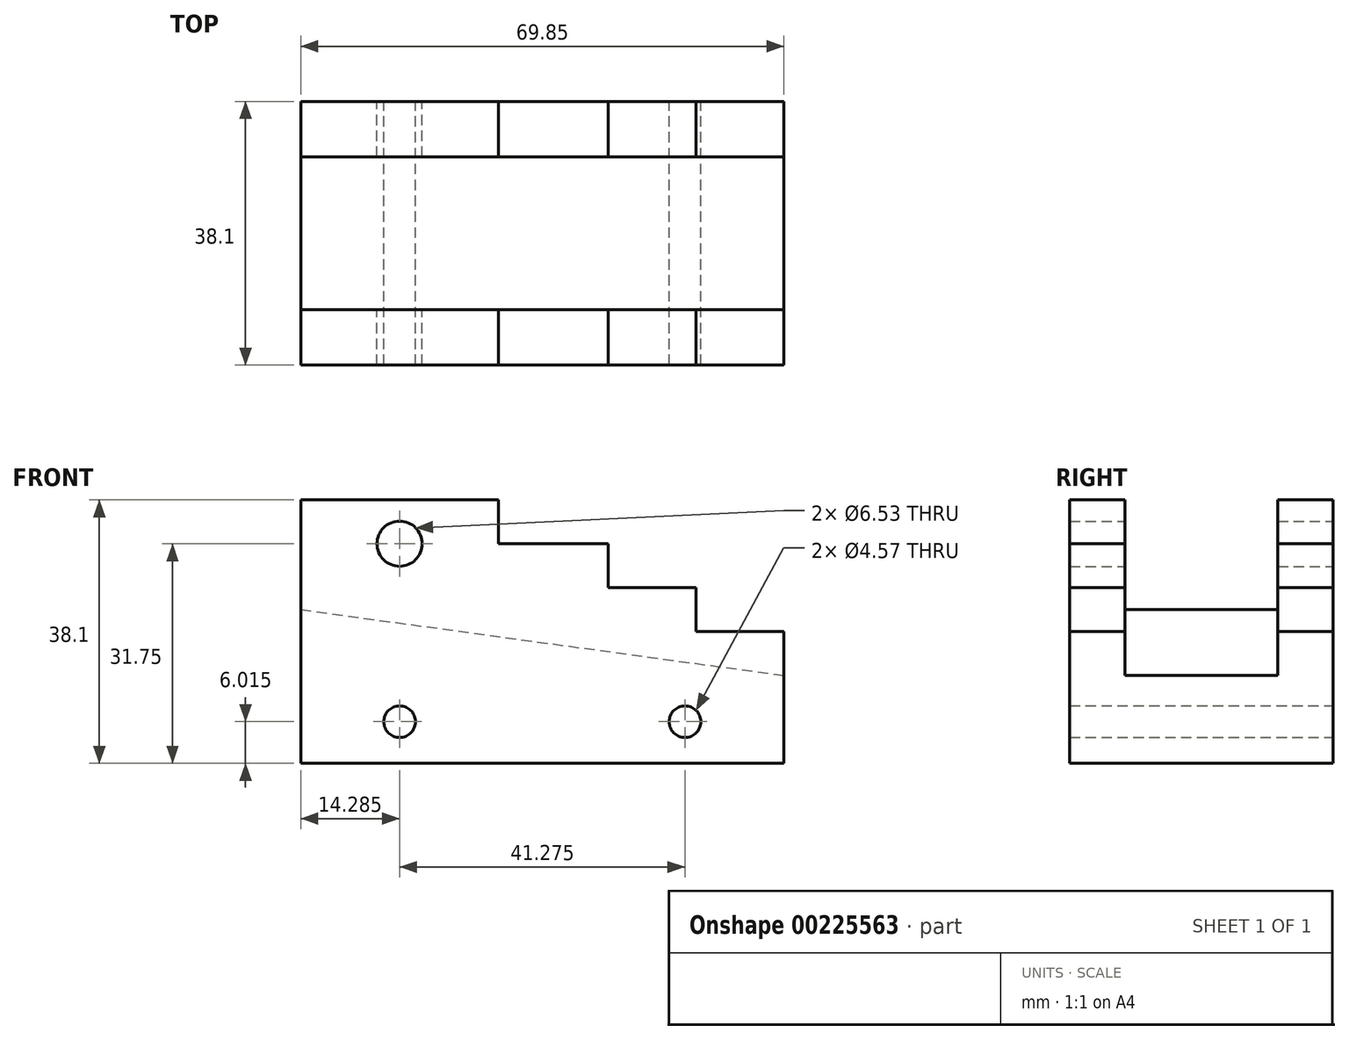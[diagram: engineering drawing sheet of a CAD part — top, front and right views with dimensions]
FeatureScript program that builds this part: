
annotation { "Feature Type Name" : "Feature", "Feature Type Description" : "" }
export const myFeature = defineFeature(function(context is Context, id is Id, definition is map)
    precondition{}
    {
        {
            var Q0;
            Q0=qCreatedBy(makeId("Front.planeOp"),FACE);
            var sketch = newSketch(context, id + "F0", { "sketchPlane" : qUnion([Q0])});
            skLineSegment(sketch, "E0", {"start": v(41.58, 0) * mm, "end": v(-28.27, 0) * mm});
            skLineSegment(sketch, "E1", {"start": v(-28.27, 0) * mm, "end": v(-28.27, 38.1) * mm});
            skLineSegment(sketch, "E2", {"start": v(-28.27, 38.1) * mm, "end": v(0.3, 38.1) * mm});
            skLineSegment(sketch, "E3", {"start": v(0.3, 38.1) * mm, "end": v(0.3, 31.75) * mm});
            skLineSegment(sketch, "E4", {"start": v(0.3, 31.75) * mm, "end": v(16.18, 31.75) * mm});
            skLineSegment(sketch, "E5", {"start": v(16.18, 31.75) * mm, "end": v(16.18, 25.4) * mm});
            skLineSegment(sketch, "E6", {"start": v(16.18, 25.4) * mm, "end": v(28.88, 25.4) * mm});
            skLineSegment(sketch, "E7", {"start": v(28.88, 25.4) * mm, "end": v(28.88, 19.05) * mm});
            skLineSegment(sketch, "E8", {"start": v(28.88, 19.05) * mm, "end": v(41.58, 19.05) * mm});
            skLineSegment(sketch, "E9", {"start": v(41.58, 19.05) * mm, "end": v(41.58, 0) * mm});
            skCircle(sketch, "E10", {"center": v(-13.99, 31.75) * mm, "radius": 3.26 * mm});
            skCircle(sketch, "E11", {"center": v(-13.99, 6.02) * mm, "radius": 2.29 * mm});
            skCircle(sketch, "E12", {"center": v(27.29, 6.02) * mm, "radius": 2.29 * mm});
            skSolve(sketch);
        }
        {
            var Q0;
            Q0 = qSketchRegion(id + "F0", true);
            extrude(context, id + "F1", {"entities" : qUnion([Q0]), "depth" : 38.1 * mm});
        }
        {
            var Q0;
            Q0=makeQuery(id+"F1.opExtrude","SWEPT_FACE",FACE,{"disambiguationData":[OSD([sQuery(id+"F0.wireOp",EDGE,"E9")])]});
            var sketch = newSketch(context, id + "F2", { "sketchPlane" : qUnion([Q0])});
            skLineSegment(sketch, "E13.0", {"start": v(-38.1, 38.1) * mm, "end": v(0, 38.1) * mm});
            skLineSegment(sketch, "E14.0", {"start": v(-38.1, 19.05) * mm, "end": v(-38.1, 0) * mm});
            skLineSegment(sketch, "E15.0", {"start": v(0, 19.05) * mm, "end": v(0, 0) * mm});
            skLineSegment(sketch, "E16.0.0", {"start": v(0, 0) * mm, "end": v(0, 19.05) * mm});
            skLineSegment(sketch, "E16.0.1", {"start": v(0, 19.05) * mm, "end": v(-38.1, 19.05) * mm});
            skLineSegment(sketch, "E16.0.3", {"start": v(-38.1, 0) * mm, "end": v(0, 0) * mm});
            skLineSegment(sketch, "E17.0.0", {"start": v(0, 19.05) * mm, "end": v(0, 25.4) * mm});
            skLineSegment(sketch, "E17.0.1", {"start": v(0, 25.4) * mm, "end": v(-38.1, 25.4) * mm});
            skLineSegment(sketch, "E17.0.2", {"start": v(-38.1, 25.4) * mm, "end": v(-38.1, 19.05) * mm});
            skLineSegment(sketch, "E17.0.3", {"start": v(-38.1, 19.05) * mm, "end": v(0, 19.05) * mm});
            skLineSegment(sketch, "E18.0.0", {"start": v(0, 25.4) * mm, "end": v(0, 31.75) * mm});
            skLineSegment(sketch, "E18.0.1", {"start": v(0, 31.75) * mm, "end": v(-38.1, 31.75) * mm});
            skLineSegment(sketch, "E18.0.2", {"start": v(-38.1, 31.75) * mm, "end": v(-38.1, 25.4) * mm});
            skLineSegment(sketch, "E18.0.3", {"start": v(-38.1, 25.4) * mm, "end": v(0, 25.4) * mm});
            skLineSegment(sketch, "E19.0.0", {"start": v(0, 31.75) * mm, "end": v(0, 38.1) * mm});
            skLineSegment(sketch, "E19.0.1", {"start": v(0, 38.1) * mm, "end": v(-38.1, 38.1) * mm});
            skLineSegment(sketch, "E19.0.2", {"start": v(-38.1, 38.1) * mm, "end": v(-38.1, 31.75) * mm});
            skLineSegment(sketch, "E19.0.3", {"start": v(-38.1, 31.75) * mm, "end": v(0, 31.75) * mm});
            skLineSegment(sketch, "E20.0.0", {"start": v(0, 38.1) * mm, "end": v(0, 0) * mm});
            skLineSegment(sketch, "E20.0.1", {"start": v(0, 0) * mm, "end": v(-38.1, 0) * mm});
            skLineSegment(sketch, "E20.0.2", {"start": v(-38.1, 0) * mm, "end": v(-38.1, 38.1) * mm});
            skLineSegment(sketch, "E21.0", {"start": v(0, 0) * mm, "end": v(0, 38.1) * mm});
            skLineSegment(sketch, "E22", {"start": v(-30.1, 12.7) * mm, "end": v(-8, 12.7) * mm});
            skLineSegment(sketch, "E23", {"start": v(-30.1, 12.7) * mm, "end": v(-30.1, 38.1) * mm});
            skLineSegment(sketch, "E24", {"start": v(-30.1, 38.1) * mm, "end": v(-8, 38.1) * mm});
            skLineSegment(sketch, "E25", {"start": v(-8, 38.1) * mm, "end": v(-8, 12.7) * mm});
            skSolve(sketch);
        }
        {
            var Q0;
            Q0=makeQuery(id+"F1.opExtrude","SWEPT_FACE",FACE,{"disambiguationData":[OSD([sQuery(id+"F0.wireOp",EDGE,"E1")])]});
            var sketch = newSketch(context, id + "F3", { "sketchPlane" : qUnion([Q0])});
            skLineSegment(sketch, "E26.0", {"start": v(8, 38.1) * mm, "end": v(8, 12.7) * mm});
            skLineSegment(sketch, "E27.0", {"start": v(30.1, 12.7) * mm, "end": v(30.1, 38.1) * mm});
            skLineSegment(sketch, "E28", {"start": v(8, 22.23) * mm, "end": v(30.1, 22.23) * mm});
            skLineSegment(sketch, "E29", {"start": v(30.1, 22.23) * mm, "end": v(30.1, 38.1) * mm});
            skLineSegment(sketch, "E30", {"start": v(8, 38.1) * mm, "end": v(8, 22.23) * mm});
            skSolve(sketch);
        }
        {
            var Q0;
            Q0=makeQuery(id+"F1.opExtrude","CAP_FACE",FACE,{"disambiguationData":[OSD([sQuery(id+"F0.wireOp",EDGE,"E0"),sQuery(id+"F0.wireOp",EDGE,"E1"),sQuery(id+"F0.wireOp",EDGE,"E2"),sQuery(id+"F0.wireOp",EDGE,"E3"),sQuery(id+"F0.wireOp",EDGE,"E4"),sQuery(id+"F0.wireOp",EDGE,"E5"),sQuery(id+"F0.wireOp",EDGE,"E6"),sQuery(id+"F0.wireOp",EDGE,"E7"),sQuery(id+"F0.wireOp",EDGE,"E8"),sQuery(id+"F0.wireOp",EDGE,"E9"),sQuery(id+"F0.wireOp",EDGE,"E10"),sQuery(id+"F0.wireOp",EDGE,"E11"),sQuery(id+"F0.wireOp",EDGE,"E12")])],"isStart":false});
            cPlane(context, id + "F4", {"entities" : qUnion([Q0]), "cplaneType" : CPlaneType.OFFSET, "offset" : 8 * mm, "oppositeDirection" : true, "width" : 152.4 * mm, "height" : 152.4 * mm});
        }
        {
            var Q0;
            Q0=qCreatedBy(id+"F4.planeOp",FACE);
            var sketch = newSketch(context, id + "F5", { "sketchPlane" : qUnion([Q0])});
            skLineSegment(sketch, "E31.0", {"start": v(-28.27, 22.23) * mm, "end": v(-28.27, 38.1) * mm});
            skLineSegment(sketch, "E32.0", {"start": v(41.58, 12.7) * mm, "end": v(41.58, 38.1) * mm});
            skLineSegment(sketch, "E33", {"start": v(-28.27, 22.22) * mm, "end": v(41.58, 12.7) * mm});
            skLineSegment(sketch, "E34", {"start": v(-28.27, 38.1) * mm, "end": v(41.58, 38.1) * mm});
            skSolve(sketch);
        }
        {
            var Q0;
            Q0=makeQuery(id+"F5.imprint","IMPRINT",FACE,{"disambiguationData":[TD([[makeQuery(id+"F5.imprint","IMPRINT",EDGE,{"derivedFrom":sQuery(id+"F5.wireOp",EDGE,"E31.0")}),-1.0]])]});
            extrude(context, id + "F6", {"entities" : qUnion([Q0]), "operationType" : NewBodyOperationType.REMOVE, "oppositeDirection" : true, "depth" : 22.1 * mm});
        }
    });
